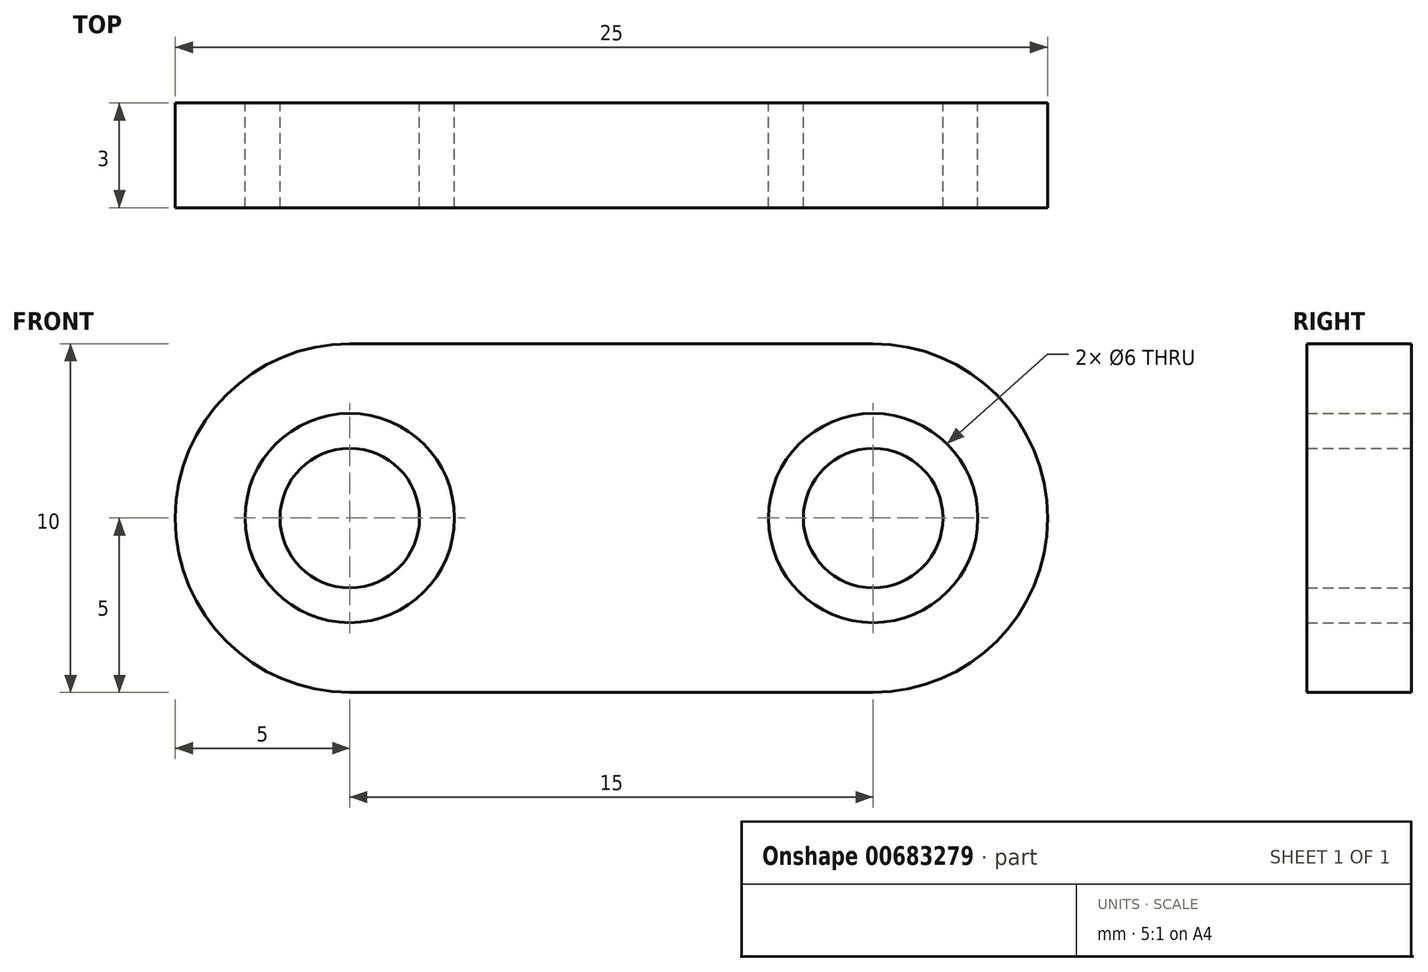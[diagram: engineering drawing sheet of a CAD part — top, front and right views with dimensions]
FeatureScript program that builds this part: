
annotation { "Feature Type Name" : "Feature", "Feature Type Description" : "" }
export const myFeature = defineFeature(function(context is Context, id is Id, definition is map)
    precondition{}
    {
        {
            var Q0;
            Q0=qCreatedBy(makeId("Front.planeOp"),FACE);
            var sketch = newSketch(context, id + "F0", { "sketchPlane" : qUnion([Q0])});
            skCircle(sketch, "E0", {"center": v(-7.5, 0) * mm, "radius": 3 * mm});
            skCircle(sketch, "E1", {"center": v(7.5, 0) * mm, "radius": 3 * mm});
            skArc(sketch, "E2", {"start": v(-7.5, 5) * mm, "mid": v(-12.5, 0) * mm, "end": v(-7.5, -5) * mm});
            skCircle(sketch, "E3", {"center": v(-7.5, 0) * mm, "radius": 2 * mm});
            skArc(sketch, "E4", {"start": v(7.5, -5) * mm, "mid": v(12.5, 0) * mm, "end": v(7.5, 5) * mm});
            skCircle(sketch, "E5", {"center": v(7.5, 0) * mm, "radius": 2 * mm});
            skLineSegment(sketch, "E6", {"start": v(-7.5, 5) * mm, "end": v(7.5, 5) * mm});
            skLineSegment(sketch, "E7", {"start": v(-7.5, -5) * mm, "end": v(7.5, -5) * mm});
            skSolve(sketch);
        }
        {
            var Q0;
            Q0 = qSketchRegion(id + "F0", true);
            var Q1;
            Q1=makeQuery(id+"F0.imprint","IMPRINT",FACE,{"disambiguationData":[TD([[makeQuery(id+"F0.imprint","IMPRINT",EDGE,{"derivedFrom":sQuery(id+"F0.wireOp",EDGE,"E3")}),1.0]])]});
            var Q2;
            Q2=makeQuery(id+"F0.imprint","IMPRINT",FACE,{"disambiguationData":[TD([[makeQuery(id+"F0.imprint","IMPRINT",EDGE,{"derivedFrom":sQuery(id+"F0.wireOp",EDGE,"E5")}),1.0]])]});
            extrude(context, id + "F1", {"entities" : qUnion([Q0, Q1, Q2]), "depth" : 3 * mm, "offsetDistance" : 25 * mm});
        }
    });
